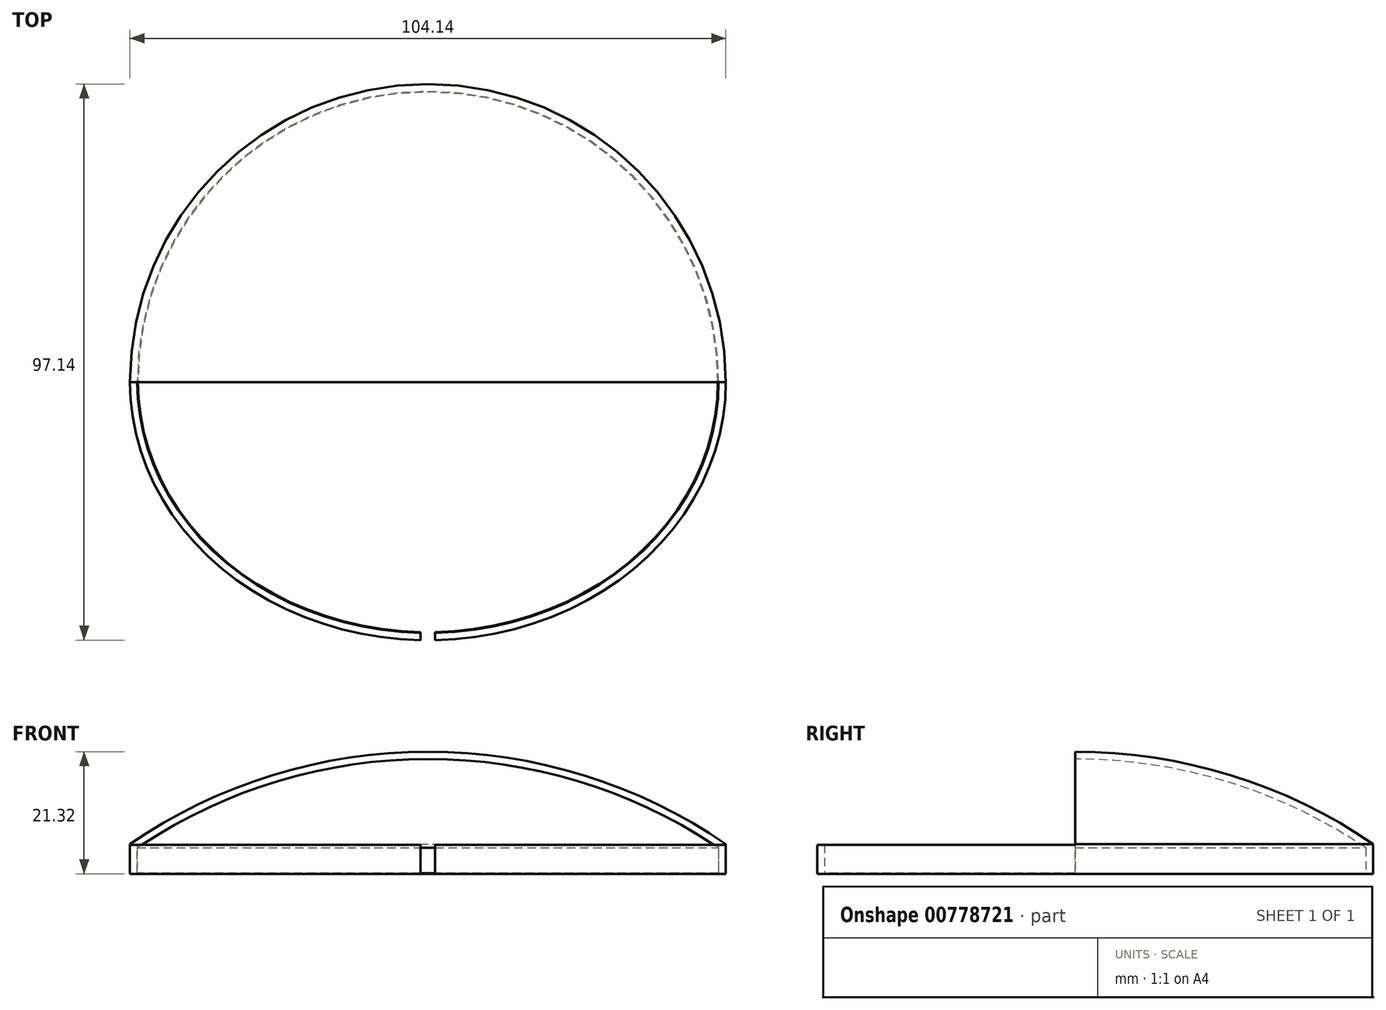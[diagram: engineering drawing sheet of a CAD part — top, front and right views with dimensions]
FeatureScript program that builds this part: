
annotation { "Feature Type Name" : "Feature", "Feature Type Description" : "" }
export const myFeature = defineFeature(function(context is Context, id is Id, definition is map)
    precondition{}
    {
        {
            var Q0;
            Q0=qCreatedBy(makeId("Front.planeOp"),FACE);
            var sketch = newSketch(context, id + "F0", { "sketchPlane" : qUnion([Q0])});
            skLineSegment(sketch, "E0", {"start": v(0, 0) * mm, "end": v(0, 69.58) * mm, "construction": true});
            skLineSegment(sketch, "E1", {"start": v(52.07, 0) * mm, "end": v(52.07, 5.2) * mm});
            skArc(sketch, "E2", {"start": v(52.07, 5.2) * mm, "mid": v(27.25, 17.2) * mm, "end": v(0, 21.32) * mm});
            skLineSegment(sketch, "E3", {"start": v(50.67, 0) * mm, "end": v(52.07, 0) * mm});
            skLineSegment(sketch, "E4", {"start": v(50.67, 0) * mm, "end": v(50.67, 0.13) * mm});
            skLineSegment(sketch, "E5", {"start": v(50.67, 0.13) * mm, "end": v(50.81, 0.13) * mm});
            skLineSegment(sketch, "E6", {"start": v(50.81, 0.13) * mm, "end": v(50.81, 4.53) * mm});
            skArc(sketch, "E7.0", {"start": v(50.81, 4.53) * mm, "mid": v(26.56, 16.08) * mm, "end": v(0, 20.05) * mm});
            skLineSegment(sketch, "E8", {"start": v(0, 21.32) * mm, "end": v(0, 20.05) * mm});
            skSolve(sketch);
        }
        {
            var Q0;
            Q0 = qSketchRegion(id + "F0", true);
            var Q1;
            Q1=sQuery(id+"F0.wireOp",EDGE,"E0");
            revolve(context, id + "F1", {"surfaceOperationType" : NewSurfaceOperationType.NEW, "entities" : qUnion([Q0]), "axis" : qUnion([Q1]), "revolveType" : RevolveType.ONE_DIRECTION, "angle" : 180 * degree});
        }
        {
            var Q0;
            Q0=qCreatedBy(makeId("Top.planeOp"),FACE);
            var sketch = newSketch(context, id + "F2", { "sketchPlane" : qUnion([Q0])});
            skEllipticalArc(sketch, "E9", {});
            const initialGuessF2  = {"E9": [0, 0, 1, 0, 0.05207, 0.045085, 3.141592653589793, 0]};
            skSetInitialGuess(sketch, initialGuessF2);
            skSolve(sketch);
        }
        {
            var Q0;
            Q0=qCreatedBy(makeId("Front.planeOp"),FACE);
            var sketch = newSketch(context, id + "F3", { "sketchPlane" : qUnion([Q0])});
            skLineSegment(sketch, "E10", {"start": v(52.07, 0) * mm, "end": v(52.07, 5.08) * mm});
            skLineSegment(sketch, "E11", {"start": v(50.8, 5.08) * mm, "end": v(50.8, 0.13) * mm});
            skLineSegment(sketch, "E12", {"start": v(50.8, 0.13) * mm, "end": v(50.67, 0.13) * mm});
            skLineSegment(sketch, "E13", {"start": v(50.67, 0.13) * mm, "end": v(50.67, 0) * mm});
            skLineSegment(sketch, "E14", {"start": v(50.67, 0) * mm, "end": v(52.07, 0) * mm});
            skLineSegment(sketch, "E15", {"start": v(52.07, 5.08) * mm, "end": v(50.8, 5.08) * mm});
            skSolve(sketch);
        }
        {
            var Q0;
            Q0 = qSketchRegion(id + "F3", true);
            var Q1;
            Q1 = qConstructionFilter(qBodyType(qCreatedBy(id + "F2" ,EDGE), BodyType.WIRE), ConstructionObject.NO);
            sweep(context, id + "F4", {"operationType" : NewBodyOperationType.ADD, "profiles" : qUnion([Q0]), "path" : qUnion([Q1])});
        }
        {
            var Q0;
            Q0=qCreatedBy(makeId("Front.planeOp"),FACE);
            var sketch = newSketch(context, id + "F5", { "sketchPlane" : qUnion([Q0])});
            skLineSegment(sketch, "E16.bottom", {"start": v(1.27, -6.35) * mm, "end": v(-1.27, -6.35) * mm});
            skLineSegment(sketch, "E16.top", {"start": v(1.27, 6.35) * mm, "end": v(-1.27, 6.35) * mm});
            skLineSegment(sketch, "E16.left", {"start": v(1.27, -6.35) * mm, "end": v(1.27, 6.35) * mm});
            skLineSegment(sketch, "E16.right", {"start": v(-1.27, -6.35) * mm, "end": v(-1.27, 6.35) * mm});
            skPoint(sketch, "E16.middle", {"position": v(0, 0) * mm});
            skSolve(sketch);
        }
        {
            var Q0;
            Q0 = qSketchRegion(id + "F5", true);
            extrude(context, id + "F6", {"entities" : qUnion([Q0]), "operationType" : NewBodyOperationType.REMOVE, "depth" : 57.66 * mm, "offsetDistance" : 25.4 * mm});
        }
    });
